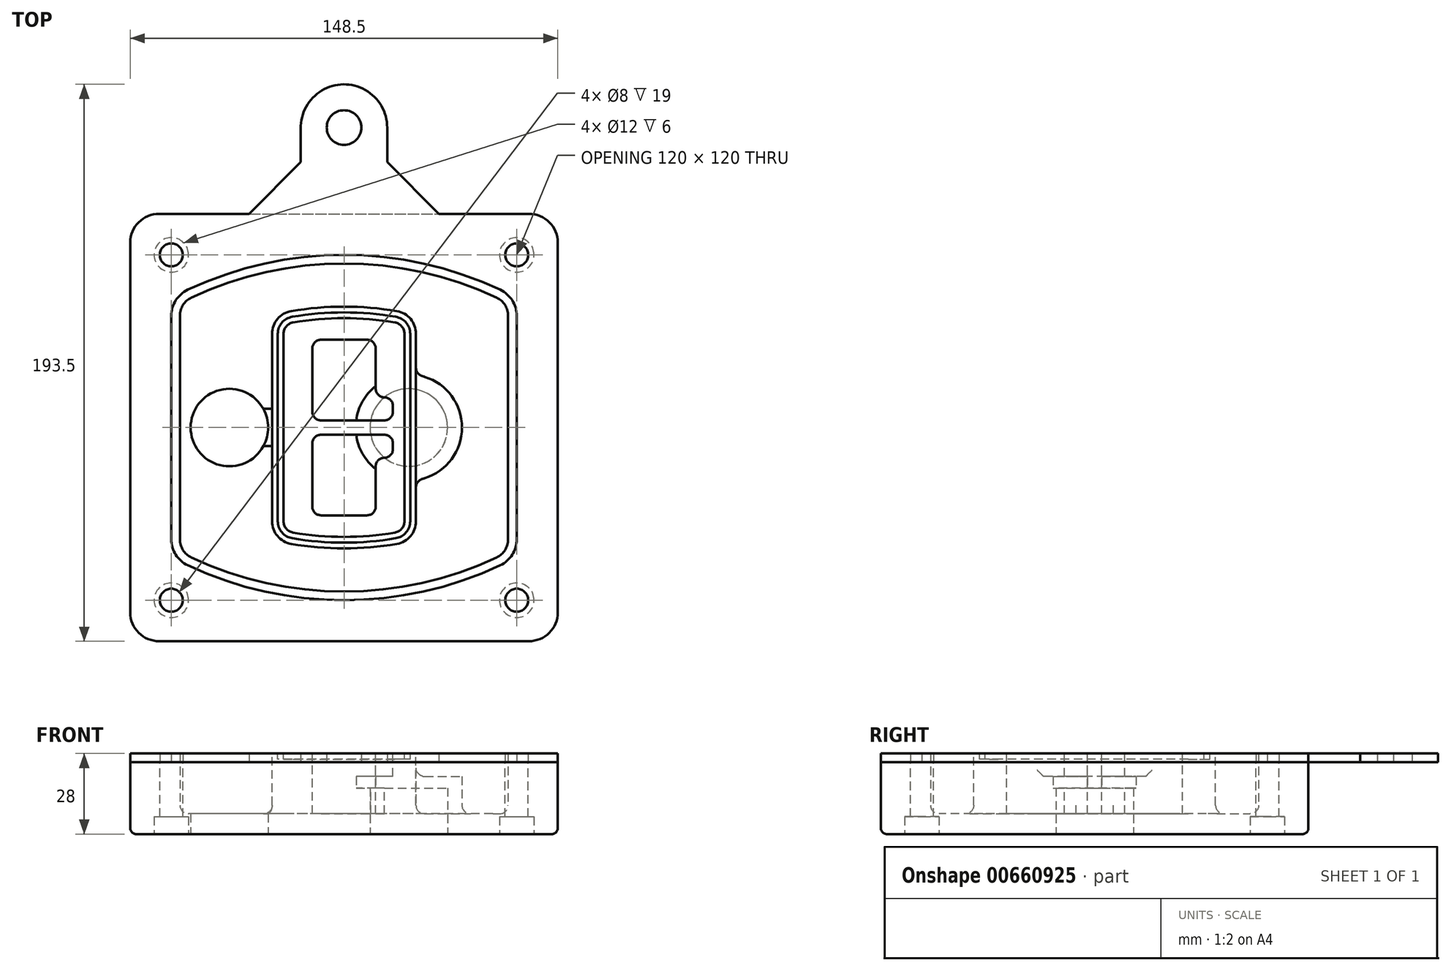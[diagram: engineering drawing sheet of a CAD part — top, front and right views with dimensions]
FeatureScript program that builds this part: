
annotation { "Feature Type Name" : "Feature", "Feature Type Description" : "" }
export const myFeature = defineFeature(function(context is Context, id is Id, definition is map)
    precondition{}
    {
        {
            var Q0;
            Q0=qCreatedBy(makeId("Top.planeOp"),FACE);
            var sketch = newSketch(context, id + "F0", { "sketchPlane" : qUnion([Q0])});
            skPoint(sketch, "E0.rect.middle", {"position": v(0, 0) * mm});
            skLineSegment(sketch, "E1.bottom", {"start": v(-64.25, -74.25) * mm, "end": v(64.25, -74.25) * mm});
            skLineSegment(sketch, "E1.top", {"start": v(-64.25, 74.25) * mm, "end": v(64.25, 74.25) * mm});
            skLineSegment(sketch, "E1.left", {"start": v(-74.25, -64.25) * mm, "end": v(-74.25, 64.25) * mm});
            skLineSegment(sketch, "E1.right", {"start": v(74.25, -64.25) * mm, "end": v(74.25, 64.25) * mm});
            skLineSegment(sketch, "E2", {"start": v(-74.25, 74.25) * mm, "end": v(74.25, -74.25) * mm, "construction": true});
            skLineSegment(sketch, "E3", {"start": v(74.25, 74.25) * mm, "end": v(-74.25, -74.25) * mm, "construction": true});
            skCircle(sketch, "E4", {"center": v(-60, 60) * mm, "radius": 4 * mm});
            skCircle(sketch, "E5", {"center": v(60, 60) * mm, "radius": 4 * mm});
            skCircle(sketch, "E6", {"center": v(60, -60) * mm, "radius": 4 * mm});
            skCircle(sketch, "E7", {"center": v(-60, -60) * mm, "radius": 4 * mm});
            skLineSegment(sketch, "E8", {"start": v(-60, 60) * mm, "end": v(60, 60) * mm, "construction": true});
            skLineSegment(sketch, "E9", {"start": v(60, 60) * mm, "end": v(60, -60) * mm, "construction": true});
            skLineSegment(sketch, "E10", {"start": v(60, -60) * mm, "end": v(-60, -60) * mm, "construction": true});
            skLineSegment(sketch, "E11", {"start": v(-60, -60) * mm, "end": v(-60, 60) * mm, "construction": true});
            skLineSegment(sketch, "E12", {"start": v(-60, 38.83) * mm, "end": v(-60, -38.83) * mm});
            skLineSegment(sketch, "E13", {"start": v(60, 38.83) * mm, "end": v(60, -38.83) * mm});
            skArc(sketch, "E14", {"start": v(54.26, 47.88) * mm, "mid": v(0, 60) * mm, "end": v(-54.26, 47.88) * mm});
            skArc(sketch, "E15", {"start": v(-54.26, -47.88) * mm, "mid": v(0, -60) * mm, "end": v(54.26, -47.88) * mm});
            skLineSegment(sketch, "E16", {"start": v(-60, 0) * mm, "end": v(60, 0) * mm, "construction": true});
            skPoint(sketch, "E17.visualSharp", {"position": v(-60, -45) * mm});
            skArc(sketch, "E17.filletArc", {"start": v(-60, -38.83) * mm, "mid": v(-58.44, -44.2) * mm, "end": v(-54.26, -47.88) * mm});
            skPoint(sketch, "E18.visualSharp", {"position": v(-60, 45) * mm});
            skArc(sketch, "E18.filletArc", {"start": v(-54.26, 47.88) * mm, "mid": v(-58.44, 44.2) * mm, "end": v(-60, 38.83) * mm});
            skPoint(sketch, "E19.visualSharp", {"position": v(60, 45) * mm});
            skArc(sketch, "E19.filletArc", {"start": v(60, 38.83) * mm, "mid": v(58.44, 44.2) * mm, "end": v(54.26, 47.88) * mm});
            skPoint(sketch, "E20.visualSharp", {"position": v(60, -45) * mm});
            skArc(sketch, "E20.filletArc", {"start": v(54.26, -47.88) * mm, "mid": v(58.44, -44.2) * mm, "end": v(60, -38.83) * mm});
            skPoint(sketch, "E21.visualSharp", {"position": v(-74.25, 74.25) * mm});
            skArc(sketch, "E21.filletArc", {"start": v(-64.25, 74.25) * mm, "mid": v(-71.32, 71.32) * mm, "end": v(-74.25, 64.25) * mm});
            skPoint(sketch, "E22.visualSharp", {"position": v(74.25, 74.25) * mm});
            skArc(sketch, "E22.filletArc", {"start": v(74.25, 64.25) * mm, "mid": v(71.32, 71.32) * mm, "end": v(64.25, 74.25) * mm});
            skPoint(sketch, "E23.visualSharp", {"position": v(74.25, -74.25) * mm});
            skArc(sketch, "E23.filletArc", {"start": v(64.25, -74.25) * mm, "mid": v(71.32, -71.32) * mm, "end": v(74.25, -64.25) * mm});
            skPoint(sketch, "E24.visualSharp", {"position": v(-74.25, -74.25) * mm});
            skArc(sketch, "E24.filletArc", {"start": v(-74.25, -64.25) * mm, "mid": v(-71.32, -71.32) * mm, "end": v(-64.25, -74.25) * mm});
            skArc(sketch, "E25.0", {"start": v(57, 38.83) * mm, "mid": v(55.9, 42.58) * mm, "end": v(52.98, 45.17) * mm});
            skLineSegment(sketch, "E25.1", {"start": v(57, 38.83) * mm, "end": v(57, -38.83) * mm});
            skArc(sketch, "E25.2", {"start": v(52.98, -45.17) * mm, "mid": v(55.9, -42.58) * mm, "end": v(57, -38.83) * mm});
            skArc(sketch, "E25.3", {"start": v(-52.98, -45.17) * mm, "mid": v(0, -57) * mm, "end": v(52.98, -45.17) * mm});
            skArc(sketch, "E25.4", {"start": v(-57, -38.83) * mm, "mid": v(-55.9, -42.58) * mm, "end": v(-52.98, -45.17) * mm});
            skArc(sketch, "E25.5", {"start": v(52.98, 45.17) * mm, "mid": v(0, 57) * mm, "end": v(-52.98, 45.17) * mm});
            skLineSegment(sketch, "E25.6", {"start": v(-57, 38.83) * mm, "end": v(-57, -38.83) * mm});
            skArc(sketch, "E25.7", {"start": v(-52.98, 45.17) * mm, "mid": v(-55.9, 42.58) * mm, "end": v(-57, 38.83) * mm});
            skArc(sketch, "E26.0", {"start": v(-55.96, 51.5) * mm, "mid": v(-61.82, 46.33) * mm, "end": v(-64, 38.83) * mm});
            skArc(sketch, "E26.1", {"start": v(55.96, 51.5) * mm, "mid": v(0, 64) * mm, "end": v(-55.96, 51.5) * mm});
            skArc(sketch, "E26.2", {"start": v(64, 38.83) * mm, "mid": v(61.82, 46.33) * mm, "end": v(55.96, 51.5) * mm});
            skLineSegment(sketch, "E26.3", {"start": v(64, 38.83) * mm, "end": v(64, -38.83) * mm});
            skArc(sketch, "E26.4", {"start": v(55.96, -51.5) * mm, "mid": v(61.82, -46.33) * mm, "end": v(64, -38.83) * mm});
            skLineSegment(sketch, "E26.5", {"start": v(-64, 38.83) * mm, "end": v(-64, -38.83) * mm});
            skArc(sketch, "E26.6", {"start": v(-55.96, -51.5) * mm, "mid": v(0, -64) * mm, "end": v(55.96, -51.5) * mm});
            skArc(sketch, "E26.7", {"start": v(-64, -38.83) * mm, "mid": v(-61.82, -46.33) * mm, "end": v(-55.96, -51.5) * mm});
            skSolve(sketch);
        }
        {
            var Q0;
            Q0=makeQuery(id+"F0.imprint","IMPRINT",FACE,{"disambiguationData":[TD([[makeQuery(id+"F0.imprint","IMPRINT",EDGE,{"derivedFrom":sQuery(id+"F0.wireOp",EDGE,"E1.bottom")}),1.0]])]});
            var Q1;
            Q1=makeQuery(id+"F0.imprint","IMPRINT",FACE,{"disambiguationData":[TD([[makeQuery(id+"F0.imprint","IMPRINT",EDGE,{"derivedFrom":sQuery(id+"F0.wireOp",EDGE,"E12")}),1.0]])]});
            var Q2;
            Q2=makeQuery(id+"F0.imprint","IMPRINT",FACE,{"disambiguationData":[TD([[makeQuery(id+"F0.imprint","IMPRINT",EDGE,{"derivedFrom":sQuery(id+"F0.wireOp",EDGE,"E25.0")}),1.0]])]});
            var Q3;
            Q3=makeQuery(id+"F0.imprint","IMPRINT",FACE,{"disambiguationData":[TD([[makeQuery(id+"F0.imprint","IMPRINT",EDGE,{"derivedFrom":sQuery(id+"F0.wireOp",EDGE,"E12")}),-1.0]])]});
            extrude(context, id + "F1", {"entities" : qUnion([Q0, Q1, Q2, Q3]), "oppositeDirection" : true, "depth" : 25 * mm});
        }
        {
            var Q0;
            Q0=makeQuery(id+"F0.imprint","IMPRINT",FACE,{"disambiguationData":[TD([[makeQuery(id+"F0.imprint","IMPRINT",EDGE,{"derivedFrom":sQuery(id+"F0.wireOp",EDGE,"E12")}),1.0]])]});
            extrude(context, id + "F2", {"entities" : qUnion([Q0]), "operationType" : NewBodyOperationType.ADD, "depth" : 3 * mm});
        }
        {
            var Q0;
            Q0=makeQuery(id+"F0.imprint","IMPRINT",FACE,{"disambiguationData":[TD([[makeQuery(id+"F0.imprint","IMPRINT",EDGE,{"derivedFrom":sQuery(id+"F0.wireOp",EDGE,"E25.0")}),1.0]])]});
            extrude(context, id + "F3", {"entities" : qUnion([Q0]), "operationType" : NewBodyOperationType.REMOVE, "oppositeDirection" : true, "depth" : 18 * mm});
        }
        {
            var Q0;
            Q0=makeQuery(id+"F2.opExtrude","CAP_FACE",FACE,{"disambiguationData":[OSD([sQuery(id+"F0.wireOp",EDGE,"E12"),sQuery(id+"F0.wireOp",EDGE,"E13"),sQuery(id+"F0.wireOp",EDGE,"E14"),sQuery(id+"F0.wireOp",EDGE,"E15"),sQuery(id+"F0.wireOp",EDGE,"E17.filletArc"),sQuery(id+"F0.wireOp",EDGE,"E18.filletArc"),sQuery(id+"F0.wireOp",EDGE,"E19.filletArc"),sQuery(id+"F0.wireOp",EDGE,"E20.filletArc"),sQuery(id+"F0.wireOp",EDGE,"E25.0"),sQuery(id+"F0.wireOp",EDGE,"E25.1"),sQuery(id+"F0.wireOp",EDGE,"E25.2"),sQuery(id+"F0.wireOp",EDGE,"E25.3"),sQuery(id+"F0.wireOp",EDGE,"E25.4"),sQuery(id+"F0.wireOp",EDGE,"E25.5"),sQuery(id+"F0.wireOp",EDGE,"E25.6"),sQuery(id+"F0.wireOp",EDGE,"E25.7")])],"isStart":false});
            var sketch = newSketch(context, id + "F4", { "sketchPlane" : qUnion([Q0])});
            skArc(sketch, "E27.0", {"start": v(-18.34, -40.45) * mm, "mid": v(0, -42) * mm, "end": v(18.34, -40.45) * mm});
            skArc(sketch, "E28.0", {"start": v(18.34, 40.45) * mm, "mid": v(0, 42) * mm, "end": v(-18.34, 40.45) * mm});
            skLineSegment(sketch, "E29", {"start": v(-25, 32.57) * mm, "end": v(-25, -32.57) * mm});
            skLineSegment(sketch, "E30", {"start": v(25, 32.57) * mm, "end": v(25, -32.57) * mm});
            skLineSegment(sketch, "E31", {"start": v(-25, 39.1) * mm, "end": v(25, 39.1) * mm, "construction": true});
            skLineSegment(sketch, "E32", {"start": v(-25, -39.1) * mm, "end": v(25, -39.1) * mm, "construction": true});
            skPoint(sketch, "E33.visualSharp", {"position": v(-25, 39.1) * mm});
            skArc(sketch, "E33.filletArc", {"start": v(-18.34, 40.45) * mm, "mid": v(-23.11, 37.73) * mm, "end": v(-25, 32.57) * mm});
            skPoint(sketch, "E34.visualSharp", {"position": v(25, 39.1) * mm});
            skArc(sketch, "E34.filletArc", {"start": v(25, 32.57) * mm, "mid": v(23.11, 37.73) * mm, "end": v(18.34, 40.45) * mm});
            skPoint(sketch, "E35.visualSharp", {"position": v(25, -39.1) * mm});
            skArc(sketch, "E35.filletArc", {"start": v(18.34, -40.45) * mm, "mid": v(23.11, -37.73) * mm, "end": v(25, -32.57) * mm});
            skPoint(sketch, "E36.visualSharp", {"position": v(-25, -39.1) * mm});
            skArc(sketch, "E36.filletArc", {"start": v(-25, -32.57) * mm, "mid": v(-23.11, -37.73) * mm, "end": v(-18.34, -40.45) * mm});
            skArc(sketch, "E37.0", {"start": v(52.98, 45.17) * mm, "mid": v(0, 57) * mm, "end": v(-52.98, 45.17) * mm});
            skArc(sketch, "E37.1", {"start": v(-52.98, 45.17) * mm, "mid": v(-55.9, 42.58) * mm, "end": v(-57, 38.83) * mm});
            skLineSegment(sketch, "E37.2", {"start": v(-57, 38.83) * mm, "end": v(-57, -38.83) * mm});
            skArc(sketch, "E37.3", {"start": v(-57, -38.83) * mm, "mid": v(-55.9, -42.58) * mm, "end": v(-52.98, -45.17) * mm});
            skArc(sketch, "E37.4", {"start": v(-52.98, -45.17) * mm, "mid": v(0, -57) * mm, "end": v(52.98, -45.17) * mm});
            skArc(sketch, "E37.5", {"start": v(52.98, -45.17) * mm, "mid": v(55.9, -42.58) * mm, "end": v(57, -38.83) * mm});
            skLineSegment(sketch, "E37.6", {"start": v(57, 38.83) * mm, "end": v(57, -38.83) * mm});
            skArc(sketch, "E37.7", {"start": v(57, 38.83) * mm, "mid": v(55.9, 42.58) * mm, "end": v(52.98, 45.17) * mm});
            skLineSegment(sketch, "E38.0", {"start": v(23, 32.57) * mm, "end": v(23, -32.57) * mm});
            skArc(sketch, "E38.1", {"start": v(18, -38.48) * mm, "mid": v(21.58, -36.44) * mm, "end": v(23, -32.57) * mm});
            skArc(sketch, "E38.2", {"start": v(-18, -38.48) * mm, "mid": v(0, -40) * mm, "end": v(18, -38.48) * mm});
            skArc(sketch, "E38.3", {"start": v(-23, -32.57) * mm, "mid": v(-21.58, -36.44) * mm, "end": v(-18, -38.48) * mm});
            skLineSegment(sketch, "E38.4", {"start": v(-23, 32.57) * mm, "end": v(-23, -32.57) * mm});
            skArc(sketch, "E38.5", {"start": v(23, 32.57) * mm, "mid": v(21.58, 36.44) * mm, "end": v(18, 38.48) * mm});
            skArc(sketch, "E38.6", {"start": v(-18, 38.48) * mm, "mid": v(-21.58, 36.44) * mm, "end": v(-23, 32.57) * mm});
            skArc(sketch, "E38.7", {"start": v(18, 38.48) * mm, "mid": v(0, 40) * mm, "end": v(-18, 38.48) * mm});
            skArc(sketch, "E39.0", {"start": v(21, 32.57) * mm, "mid": v(20.06, 35.15) * mm, "end": v(17.67, 36.5) * mm});
            skLineSegment(sketch, "E39.1", {"start": v(21, 32.57) * mm, "end": v(21, -32.57) * mm});
            skArc(sketch, "E39.2", {"start": v(17.67, -36.5) * mm, "mid": v(20.06, -35.15) * mm, "end": v(21, -32.57) * mm});
            skArc(sketch, "E39.3", {"start": v(-17.67, -36.5) * mm, "mid": v(0, -38) * mm, "end": v(17.67, -36.5) * mm});
            skArc(sketch, "E39.4", {"start": v(-21, -32.57) * mm, "mid": v(-20.06, -35.15) * mm, "end": v(-17.67, -36.5) * mm});
            skArc(sketch, "E39.5", {"start": v(17.67, 36.5) * mm, "mid": v(0, 38) * mm, "end": v(-17.67, 36.5) * mm});
            skLineSegment(sketch, "E39.6", {"start": v(-21, 32.57) * mm, "end": v(-21, -32.57) * mm});
            skArc(sketch, "E39.7", {"start": v(-17.67, 36.5) * mm, "mid": v(-20.06, 35.15) * mm, "end": v(-21, 32.57) * mm});
            skLineSegment(sketch, "E40", {"start": v(-25, 0) * mm, "end": v(25, 0) * mm, "construction": true});
            skLineSegment(sketch, "E41", {"start": v(-11, 5.5) * mm, "end": v(-11, 27.5) * mm});
            skLineSegment(sketch, "E42", {"start": v(-8, 30.5) * mm, "end": v(8, 30.5) * mm});
            skLineSegment(sketch, "E43", {"start": v(11, 27.5) * mm, "end": v(11, 13.5) * mm});
            skLineSegment(sketch, "E44", {"start": v(14, 10.5) * mm, "end": v(14, 10.5) * mm});
            skLineSegment(sketch, "E45", {"start": v(17, 7.5) * mm, "end": v(17, 5.5) * mm});
            skLineSegment(sketch, "E46", {"start": v(14, 2.5) * mm, "end": v(-8, 2.5) * mm});
            skPoint(sketch, "E47.visualSharp", {"position": v(-11, 30.5) * mm});
            skArc(sketch, "E47.filletArc", {"start": v(-8, 30.5) * mm, "mid": v(-10.12, 29.62) * mm, "end": v(-11, 27.5) * mm});
            skPoint(sketch, "E48.visualSharp", {"position": v(11, 30.5) * mm});
            skArc(sketch, "E48.filletArc", {"start": v(11, 27.5) * mm, "mid": v(10.12, 29.62) * mm, "end": v(8, 30.5) * mm});
            skPoint(sketch, "E49.visualSharp", {"position": v(11, 10.5) * mm});
            skArc(sketch, "E49.filletArc", {"start": v(11, 13.5) * mm, "mid": v(11.88, 11.38) * mm, "end": v(14, 10.5) * mm});
            skPoint(sketch, "E50.visualSharp", {"position": v(17, 10.5) * mm});
            skArc(sketch, "E50.filletArc", {"start": v(17, 7.5) * mm, "mid": v(16.12, 9.62) * mm, "end": v(14, 10.5) * mm});
            skPoint(sketch, "E51.visualSharp", {"position": v(17, 2.5) * mm});
            skArc(sketch, "E51.filletArc", {"start": v(14, 2.5) * mm, "mid": v(16.12, 3.38) * mm, "end": v(17, 5.5) * mm});
            skPoint(sketch, "E52.visualSharp", {"position": v(-11, 2.5) * mm});
            skArc(sketch, "E52.filletArc", {"start": v(-11, 5.5) * mm, "mid": v(-10.12, 3.38) * mm, "end": v(-8, 2.5) * mm});
            skLineSegment(sketch, "E53.0.MirrorCS", {"start": v(14, -2.5) * mm, "end": v(-8, -2.5) * mm});
            skArc(sketch, "E54.0.MirrorCS", {"start": v(-11, -5.5) * mm, "mid": v(-10.12, -3.38) * mm, "end": v(-8, -2.5) * mm});
            skLineSegment(sketch, "E55.0.MirrorCS", {"start": v(-11, -5.5) * mm, "end": v(-11, -27.5) * mm});
            skArc(sketch, "E56.0.MirrorCS", {"start": v(-8, -30.5) * mm, "mid": v(-10.12, -29.62) * mm, "end": v(-11, -27.5) * mm});
            skLineSegment(sketch, "E57.0.MirrorCS", {"start": v(-8, -30.5) * mm, "end": v(8, -30.5) * mm});
            skArc(sketch, "E58.0.MirrorCS", {"start": v(11, -27.5) * mm, "mid": v(10.12, -29.62) * mm, "end": v(8, -30.5) * mm});
            skLineSegment(sketch, "E59.0.MirrorCS", {"start": v(11, -27.5) * mm, "end": v(11, -13.5) * mm});
            skArc(sketch, "E60.0.MirrorCS", {"start": v(11, -13.5) * mm, "mid": v(11.88, -11.38) * mm, "end": v(14, -10.5) * mm});
            skArc(sketch, "E61.0.MirrorCS", {"start": v(17, -7.5) * mm, "mid": v(16.12, -9.62) * mm, "end": v(14, -10.5) * mm});
            skLineSegment(sketch, "E62.0.MirrorCS", {"start": v(17, -7.5) * mm, "end": v(17, -5.5) * mm});
            skArc(sketch, "E63.0.MirrorCS", {"start": v(14, -2.5) * mm, "mid": v(16.12, -3.38) * mm, "end": v(17, -5.5) * mm});
            skSolve(sketch);
        }
        {
            var Q0;
            Q0=makeQuery(id+"F4.imprint","IMPRINT",FACE,{"disambiguationData":[TD([[makeQuery(id+"F4.imprint","IMPRINT",EDGE,{"derivedFrom":sQuery(id+"F4.wireOp",EDGE,"E27.0")}),1.0]])]});
            var Q1;
            Q1=makeQuery(id+"F4.imprint","IMPRINT",FACE,{"disambiguationData":[TD([[makeQuery(id+"F4.imprint","IMPRINT",EDGE,{"derivedFrom":sQuery(id+"F4.wireOp",EDGE,"E38.0")}),-1.0]])]});
            var Q2;
            Q2=makeQuery(id+"F4.imprint","IMPRINT",FACE,{"disambiguationData":[TD([[makeQuery(id+"F4.imprint","IMPRINT",EDGE,{"derivedFrom":sQuery(id+"F4.wireOp",EDGE,"E39.0")}),1.0]])]});
            extrude(context, id + "F5", {"entities" : qUnion([Q0, Q1, Q2]), "operationType" : NewBodyOperationType.ADD, "endBound" : BoundingType.UP_TO_NEXT, "oppositeDirection" : true, "depth" : 25 * mm});
        }
        {
            var Q0;
            Q0=makeQuery(id+"F4.imprint","IMPRINT",FACE,{"disambiguationData":[TD([[makeQuery(id+"F4.imprint","IMPRINT",EDGE,{"derivedFrom":sQuery(id+"F4.wireOp",EDGE,"E38.0")}),-1.0]])]});
            extrude(context, id + "F6", {"entities" : qUnion([Q0]), "operationType" : NewBodyOperationType.REMOVE, "oppositeDirection" : true, "depth" : 2 * mm});
        }
        {
            var Q0;
            Q0=makeQuery(id+"F1.opExtrude","CAP_FACE",FACE,{"disambiguationData":[OSD([sQuery(id+"F0.wireOp",EDGE,"E1.bottom"),sQuery(id+"F0.wireOp",EDGE,"E1.top"),sQuery(id+"F0.wireOp",EDGE,"E1.left"),sQuery(id+"F0.wireOp",EDGE,"E1.right"),sQuery(id+"F0.wireOp",EDGE,"E4"),sQuery(id+"F0.wireOp",EDGE,"E5"),sQuery(id+"F0.wireOp",EDGE,"E6"),sQuery(id+"F0.wireOp",EDGE,"E7"),sQuery(id+"F0.wireOp",EDGE,"E21.filletArc"),sQuery(id+"F0.wireOp",EDGE,"E22.filletArc"),sQuery(id+"F0.wireOp",EDGE,"E23.filletArc"),sQuery(id+"F0.wireOp",EDGE,"E24.filletArc")])],"isStart":false});
            var sketch = newSketch(context, id + "F7", { "sketchPlane" : qUnion([Q0])});
            skCircle(sketch, "E64", {"center": v(22.5, 0) * mm, "radius": 13.47 * mm});
            skCircle(sketch, "E65", {"center": v(-39.81, 0) * mm, "radius": 13.47 * mm});
            skLineSegment(sketch, "E66", {"start": v(74.25, 0) * mm, "end": v(-74.25, 0) * mm});
            skCircle(sketch, "E67", {"center": v(22.5, 0) * mm, "radius": 18.47 * mm});
            skCircle(sketch, "E68", {"center": v(60, -60) * mm, "radius": 6 * mm});
            skCircle(sketch, "E69", {"center": v(-60, -60) * mm, "radius": 6 * mm});
            skCircle(sketch, "E70", {"center": v(-60, 60) * mm, "radius": 6 * mm});
            skCircle(sketch, "E71", {"center": v(60, 60) * mm, "radius": 6 * mm});
            skSolve(sketch);
        }
        {
            var Q0;
            {var subQ1=sQuery(id+"F7.wireOp",EDGE,"E66");var subQ4=sQuery(id+"F7.wireOp",EDGE,"E64");var subQ6=makeQuery(id+"F7.imprint","INTERSECT",VERTEX,{"disambiguationData":[OD(0.0)],"derivedFrom":[subQ4,subQ1]});Q0=makeQuery(id+"F7.imprint","IMPRINT",FACE,{"disambiguationData":[TD([[makeQuery(id+"F7.imprint","IMPRINT",EDGE,{"disambiguationData":[TD([[subQ6,-1.0]])],"derivedFrom":subQ4}),-1.0]])]});}
            var Q1;
            {var subQ0=sQuery(id+"F7.wireOp",EDGE,"E66");var subQ1=sQuery(id+"F7.wireOp",EDGE,"E64");var subQ3=makeQuery(id+"F7.imprint","INTERSECT",VERTEX,{"disambiguationData":[OD(0.0)],"derivedFrom":[subQ1,subQ0]});Q1=makeQuery(id+"F7.imprint","IMPRINT",FACE,{"disambiguationData":[TD([[makeQuery(id+"F7.imprint","IMPRINT",EDGE,{"disambiguationData":[TD([[subQ3,-1.0]])],"derivedFrom":subQ1}),1.0]])]});}
            var Q2;
            {var subQ0=sQuery(id+"F7.wireOp",EDGE,"E66");var subQ1=sQuery(id+"F7.wireOp",EDGE,"E64");var subQ3=makeQuery(id+"F7.imprint","INTERSECT",VERTEX,{"disambiguationData":[OD(0.0)],"derivedFrom":[subQ1,subQ0]});Q2=makeQuery(id+"F7.imprint","IMPRINT",FACE,{"disambiguationData":[TD([[makeQuery(id+"F7.imprint","IMPRINT",EDGE,{"disambiguationData":[TD([[subQ3,1.0]])],"derivedFrom":subQ1}),1.0]])]});}
            var Q3;
            {var subQ1=sQuery(id+"F7.wireOp",EDGE,"E66");var subQ4=sQuery(id+"F7.wireOp",EDGE,"E64");var subQ6=makeQuery(id+"F7.imprint","INTERSECT",VERTEX,{"disambiguationData":[OD(0.0)],"derivedFrom":[subQ4,subQ1]});Q3=makeQuery(id+"F7.imprint","IMPRINT",FACE,{"disambiguationData":[TD([[makeQuery(id+"F7.imprint","IMPRINT",EDGE,{"disambiguationData":[TD([[subQ6,1.0]])],"derivedFrom":subQ4}),-1.0]])]});}
            extrude(context, id + "F8", {"entities" : qUnion([Q0, Q1, Q2, Q3]), "operationType" : NewBodyOperationType.ADD, "oppositeDirection" : true, "depth" : 20 * mm});
        }
        {
            var Q0;
            {var subQ0=sQuery(id+"F7.wireOp",EDGE,"E66");var subQ1=sQuery(id+"F7.wireOp",EDGE,"E64");var subQ3=makeQuery(id+"F7.imprint","INTERSECT",VERTEX,{"disambiguationData":[OD(0.0)],"derivedFrom":[subQ1,subQ0]});Q0=makeQuery(id+"F7.imprint","IMPRINT",FACE,{"disambiguationData":[TD([[makeQuery(id+"F7.imprint","IMPRINT",EDGE,{"disambiguationData":[TD([[subQ3,-1.0]])],"derivedFrom":subQ1}),1.0]])]});}
            var Q1;
            {var subQ0=sQuery(id+"F7.wireOp",EDGE,"E66");var subQ1=sQuery(id+"F7.wireOp",EDGE,"E64");var subQ3=makeQuery(id+"F7.imprint","INTERSECT",VERTEX,{"disambiguationData":[OD(0.0)],"derivedFrom":[subQ1,subQ0]});Q1=makeQuery(id+"F7.imprint","IMPRINT",FACE,{"disambiguationData":[TD([[makeQuery(id+"F7.imprint","IMPRINT",EDGE,{"disambiguationData":[TD([[subQ3,1.0]])],"derivedFrom":subQ1}),1.0]])]});}
            extrude(context, id + "F9", {"entities" : qUnion([Q0, Q1]), "operationType" : NewBodyOperationType.REMOVE, "oppositeDirection" : true, "depth" : 16 * mm});
        }
        {
            var Q0;
            {var subQ0=sQuery(id+"F7.wireOp",EDGE,"E66");var subQ1=sQuery(id+"F7.wireOp",EDGE,"E65");var subQ3=makeQuery(id+"F7.imprint","INTERSECT",VERTEX,{"disambiguationData":[OD(0.0)],"derivedFrom":[subQ1,subQ0]});Q0=makeQuery(id+"F7.imprint","IMPRINT",FACE,{"disambiguationData":[TD([[makeQuery(id+"F7.imprint","IMPRINT",EDGE,{"disambiguationData":[TD([[subQ3,-1.0]])],"derivedFrom":subQ1}),1.0]])]});}
            var Q1;
            {var subQ0=sQuery(id+"F7.wireOp",EDGE,"E66");var subQ1=sQuery(id+"F7.wireOp",EDGE,"E65");var subQ3=makeQuery(id+"F7.imprint","INTERSECT",VERTEX,{"disambiguationData":[OD(0.0)],"derivedFrom":[subQ1,subQ0]});Q1=makeQuery(id+"F7.imprint","IMPRINT",FACE,{"disambiguationData":[TD([[makeQuery(id+"F7.imprint","IMPRINT",EDGE,{"disambiguationData":[TD([[subQ3,1.0]])],"derivedFrom":subQ1}),1.0]])]});}
            extrude(context, id + "F10", {"entities" : qUnion([Q0, Q1]), "operationType" : NewBodyOperationType.REMOVE, "oppositeDirection" : true, "depth" : 25 * mm});
        }
        {
            var Q0;
            Q0=makeQuery(id+"F7.imprint","IMPRINT",FACE,{"disambiguationData":[TD([[makeQuery(id+"F7.imprint","IMPRINT",EDGE,{"derivedFrom":sQuery(id+"F7.wireOp",EDGE,"E68")}),1.0]])]});
            var Q1;
            Q1=makeQuery(id+"F7.imprint","IMPRINT",FACE,{"disambiguationData":[TD([[makeQuery(id+"F7.imprint","IMPRINT",EDGE,{"derivedFrom":makeQuery(id+"F1.opExtrude","CAP_EDGE",EDGE,{"disambiguationData":[OSD([sQuery(id+"F0.wireOp",EDGE,"E5")])],"isStart":false})}),-1.0]])]});
            var Q2;
            Q2=makeQuery(id+"F7.imprint","IMPRINT",FACE,{"disambiguationData":[TD([[makeQuery(id+"F7.imprint","IMPRINT",EDGE,{"derivedFrom":sQuery(id+"F7.wireOp",EDGE,"E69")}),1.0]])]});
            var Q3;
            Q3=makeQuery(id+"F7.imprint","IMPRINT",FACE,{"disambiguationData":[TD([[makeQuery(id+"F7.imprint","IMPRINT",EDGE,{"derivedFrom":makeQuery(id+"F1.opExtrude","CAP_EDGE",EDGE,{"disambiguationData":[OSD([sQuery(id+"F0.wireOp",EDGE,"E4")])],"isStart":false})}),-1.0]])]});
            var Q4;
            Q4=makeQuery(id+"F7.imprint","IMPRINT",FACE,{"disambiguationData":[TD([[makeQuery(id+"F7.imprint","IMPRINT",EDGE,{"derivedFrom":sQuery(id+"F7.wireOp",EDGE,"E70")}),1.0]])]});
            var Q5;
            Q5=makeQuery(id+"F7.imprint","IMPRINT",FACE,{"disambiguationData":[TD([[makeQuery(id+"F7.imprint","IMPRINT",EDGE,{"derivedFrom":makeQuery(id+"F1.opExtrude","CAP_EDGE",EDGE,{"disambiguationData":[OSD([sQuery(id+"F0.wireOp",EDGE,"E7")])],"isStart":false})}),-1.0]])]});
            var Q6;
            Q6=makeQuery(id+"F7.imprint","IMPRINT",FACE,{"disambiguationData":[TD([[makeQuery(id+"F7.imprint","IMPRINT",EDGE,{"derivedFrom":sQuery(id+"F7.wireOp",EDGE,"E71")}),1.0]])]});
            var Q7;
            Q7=makeQuery(id+"F7.imprint","IMPRINT",FACE,{"disambiguationData":[TD([[makeQuery(id+"F7.imprint","IMPRINT",EDGE,{"derivedFrom":makeQuery(id+"F1.opExtrude","CAP_EDGE",EDGE,{"disambiguationData":[OSD([sQuery(id+"F0.wireOp",EDGE,"E6")])],"isStart":false})}),-1.0]])]});
            extrude(context, id + "F11", {"entities" : qUnion([Q0, Q1, Q2, Q3, Q4, Q5, Q6, Q7]), "operationType" : NewBodyOperationType.REMOVE, "oppositeDirection" : true, "depth" : 6 * mm});
        }
        {
            var Q0;
            Q0=makeQuery(id+"F9.boolean.opBoolean","COPY",FACE,{"derivedFrom":makeQuery(id+"F9.opExtrude","CAP_FACE",FACE,{"disambiguationData":[OSD([sQuery(id+"F7.wireOp",EDGE,"E64")])],"isStart":false})});
            var sketch = newSketch(context, id + "F12", { "sketchPlane" : qUnion([Q0])});
            skArc(sketch, "E72.0", {"start": v(11, 14.45) * mm, "mid": v(6.45, 9.13) * mm, "end": v(4.2, 2.5) * mm});
            skArc(sketch, "E72.1", {"start": v(4.2, -2.5) * mm, "mid": v(6.45, -9.13) * mm, "end": v(11, -14.45) * mm});
            skLineSegment(sketch, "E73", {"start": v(4.2, -2.5) * mm, "end": v(14, -2.5) * mm});
            skLineSegment(sketch, "E74.0", {"start": v(14, 2.5) * mm, "end": v(4.2, 2.5) * mm});
            skArc(sketch, "E74.1", {"start": v(14, 2.5) * mm, "mid": v(16.12, 3.38) * mm, "end": v(17, 5.5) * mm});
            skLineSegment(sketch, "E74.2", {"start": v(17, 7.5) * mm, "end": v(17, 5.5) * mm});
            skArc(sketch, "E74.3", {"start": v(17, 7.5) * mm, "mid": v(16.12, 9.62) * mm, "end": v(14, 10.5) * mm});
            skArc(sketch, "E74.4", {"start": v(11, 13.5) * mm, "mid": v(11.88, 11.38) * mm, "end": v(14, 10.5) * mm});
            skLineSegment(sketch, "E74.5", {"start": v(11, 14.45) * mm, "end": v(11, 13.5) * mm});
            skLineSegment(sketch, "E74.7", {"start": v(14, -2.5) * mm, "end": v(4.2, -2.5) * mm});
            skArc(sketch, "E74.8", {"start": v(14, -2.5) * mm, "mid": v(16.12, -3.38) * mm, "end": v(17, -5.5) * mm});
            skLineSegment(sketch, "E74.9", {"start": v(17, -7.5) * mm, "end": v(17, -5.5) * mm});
            skArc(sketch, "E74.10", {"start": v(17, -7.5) * mm, "mid": v(16.12, -9.62) * mm, "end": v(14, -10.5) * mm});
            skArc(sketch, "E74.11", {"start": v(11, -13.5) * mm, "mid": v(11.88, -11.38) * mm, "end": v(14, -10.5) * mm});
            skLineSegment(sketch, "E74.12", {"start": v(11, -14.45) * mm, "end": v(11, -13.5) * mm});
            skPoint(sketch, "E75.orphan", {"position": v(11, -27.5) * mm});
            skPoint(sketch, "E76.orphan", {"position": v(-8, -2.5) * mm});
            skPoint(sketch, "E77.orphan", {"position": v(-8, 2.5) * mm});
            skPoint(sketch, "E78.orphan", {"position": v(11, 27.5) * mm});
            skSolve(sketch);
        }
        {
            var Q0;
            {var subQ7=sQuery(id+"F12.wireOp",EDGE,"E72.0");var subQ14=sQuery(id+"F12.wireOp",EDGE,"E72.1");var subQ16=sQuery(id+"F12.wireOp",EDGE,"E74.1");var subQ18=sQuery(id+"F12.wireOp",EDGE,"E74.8");Q0=qUnion([makeQuery(id+"F12.imprint","IMPRINT",FACE,{"disambiguationData":[TD([[makeQuery(id+"F12.imprint","IMPRINT",EDGE,{"derivedFrom":subQ7}),1.0]])]}),makeQuery(id+"F12.imprint","IMPRINT",FACE,{"disambiguationData":[TD([[makeQuery(id+"F12.imprint","IMPRINT",EDGE,{"derivedFrom":subQ14}),1.0]])]}),makeQuery(id+"F12.imprint","IMPRINT",FACE,{"disambiguationData":[TD([[makeQuery(id+"F12.imprint","IMPRINT",EDGE,{"derivedFrom":subQ16}),1.0]])]}),makeQuery(id+"F12.imprint","IMPRINT",FACE,{"disambiguationData":[TD([[makeQuery(id+"F12.imprint","IMPRINT",EDGE,{"derivedFrom":subQ18}),-1.0]])]})]);}
            var Q1;
            Q1=makeQuery(id+"F5.boolean.opBoolean","SPLIT",FACE,{"disambiguationData":[TD([makeQuery(id+"F5.opExtrude","SWEPT_FACE",FACE,{"disambiguationData":[OSD([sQuery(id+"F4.wireOp",EDGE,"E41")])]})])],"derivedFrom":makeQuery(id+"F3.boolean.opBoolean","COPY",FACE,{"derivedFrom":makeQuery(id+"F3.opExtrude","CAP_FACE",FACE,{"disambiguationData":[OSD([sQuery(id+"F0.wireOp",EDGE,"E25.0"),sQuery(id+"F0.wireOp",EDGE,"E25.1"),sQuery(id+"F0.wireOp",EDGE,"E25.2"),sQuery(id+"F0.wireOp",EDGE,"E25.3"),sQuery(id+"F0.wireOp",EDGE,"E25.4"),sQuery(id+"F0.wireOp",EDGE,"E25.5"),sQuery(id+"F0.wireOp",EDGE,"E25.6"),sQuery(id+"F0.wireOp",EDGE,"E25.7")])],"isStart":false})})});
            extrude(context, id + "F13", {"entities" : qUnion([Q0]), "operationType" : NewBodyOperationType.REMOVE, "endBound" : BoundingType.UP_TO_SURFACE, "endBoundEntityFace" : qUnion([Q1]), "depth" : 25 * mm});
        }
        {
            var Q0;
            Q0=makeQuery(id+"F3.boolean.opBoolean","COPY",EDGE,{"derivedFrom":makeQuery(id+"F3.opExtrude","CAP_EDGE",EDGE,{"disambiguationData":[OSD([sQuery(id+"F0.wireOp",EDGE,"E25.6")])],"isStart":false})});
            var Q1;
            Q1=makeQuery(id+"F8.boolean.opBoolean","INTERSECT",EDGE,{"derivedFrom":[makeQuery(id+"F5.opExtrude","SWEPT_FACE",FACE,{"disambiguationData":[OSD([sQuery(id+"F4.wireOp",EDGE,"E30")])]}),makeQuery(id+"F8.opExtrude","CAP_FACE",FACE,{"disambiguationData":[OSD([sQuery(id+"F7.wireOp",EDGE,"E67")])],"isStart":false})]});
            var Q2;
            Q2=makeQuery(id+"F8.boolean.opBoolean","INTERSECT",EDGE,{"disambiguationData":[OD(1.0)],"derivedFrom":[makeQuery(id+"F5.opExtrude","SWEPT_FACE",FACE,{"disambiguationData":[OSD([sQuery(id+"F4.wireOp",EDGE,"E30")])]}),makeQuery(id+"F8.opExtrude","SWEPT_FACE",FACE,{"disambiguationData":[OSD([sQuery(id+"F7.wireOp",EDGE,"E67")])]})]});
            var Q3;
            {var subQ0=sQuery(id+"F4.wireOp",EDGE,"E30");Q3=makeQuery(id+"F8.boolean.opBoolean","SPLIT",EDGE,{"disambiguationData":[TD([makeQuery(id+"F5.opExtrude","SWEPT_FACE",FACE,{"disambiguationData":[OSD([sQuery(id+"F4.wireOp",EDGE,"E35.filletArc")])]})])],"derivedFrom":makeQuery(id+"F5.opExtrude","CAP_EDGE",EDGE,{"disambiguationData":[OSD([subQ0])],"isStart":false})});}
            var Q4;
            {var subQ0=sQuery(id+"F0.wireOp",EDGE,"E25.7");var subQ1=sQuery(id+"F0.wireOp",EDGE,"E25.1");var subQ2=sQuery(id+"F0.wireOp",EDGE,"E25.6");var subQ3=sQuery(id+"F0.wireOp",EDGE,"E25.5");var subQ4=sQuery(id+"F0.wireOp",EDGE,"E25.4");var subQ5=sQuery(id+"F0.wireOp",EDGE,"E25.0");var subQ6=sQuery(id+"F0.wireOp",EDGE,"E25.2");var subQ7=sQuery(id+"F0.wireOp",EDGE,"E25.3");Q4=makeQuery(id+"F8.boolean.opBoolean","INTERSECT",EDGE,{"derivedFrom":[makeQuery(id+"F5.boolean.opBoolean","SPLIT",FACE,{"disambiguationData":[TD([makeQuery(id+"F2.opExtrude","SWEPT_FACE",FACE,{"disambiguationData":[OSD([subQ5])]})])],"derivedFrom":makeQuery(id+"F3.boolean.opBoolean","COPY",FACE,{"derivedFrom":makeQuery(id+"F3.opExtrude","CAP_FACE",FACE,{"disambiguationData":[OSD([subQ5,subQ1,subQ6,subQ7,subQ4,subQ3,subQ2,subQ0])],"isStart":false})})}),makeQuery(id+"F8.opExtrude","SWEPT_FACE",FACE,{"disambiguationData":[OSD([sQuery(id+"F7.wireOp",EDGE,"E67")])]})]});}
            var Q5;
            Q5=makeQuery(id+"F8.boolean.opBoolean","INTERSECT",EDGE,{"disambiguationData":[OD(0.0)],"derivedFrom":[makeQuery(id+"F5.opExtrude","SWEPT_FACE",FACE,{"disambiguationData":[OSD([sQuery(id+"F4.wireOp",EDGE,"E30")])]}),makeQuery(id+"F8.opExtrude","SWEPT_FACE",FACE,{"disambiguationData":[OSD([sQuery(id+"F7.wireOp",EDGE,"E67")])]})]});
            fillet(context, id + "F14", {"entities" : qUnion([Q0, Q1, Q2, Q3, Q4, Q5]), "radius" : 3 * mm, "tangentPropagation" : true, "allowEdgeOverflow" : false});
        }
        {
            var Q0;
            Q0=makeQuery(id+"F1.opExtrude","CAP_EDGE",EDGE,{"disambiguationData":[OSD([sQuery(id+"F0.wireOp",EDGE,"E1.bottom")])],"isStart":false});
            fillet(context, id + "F15", {"entities" : qUnion([Q0]), "radius" : 2 * mm, "tangentPropagation" : true, "allowEdgeOverflow" : false});
        }
        {
            var Q0;
            {var subQ0=sQuery(id+"F0.wireOp",EDGE,"E21.filletArc");var subQ1=sQuery(id+"F0.wireOp",EDGE,"E7");var subQ2=sQuery(id+"F0.wireOp",EDGE,"E6");var subQ3=sQuery(id+"F0.wireOp",EDGE,"E5");var subQ4=sQuery(id+"F0.wireOp",EDGE,"E4");var subQ5=sQuery(id+"F0.wireOp",EDGE,"E22.filletArc");var subQ6=sQuery(id+"F0.wireOp",EDGE,"E1.bottom");var subQ7=sQuery(id+"F0.wireOp",EDGE,"E1.right");var subQ8=sQuery(id+"F0.wireOp",EDGE,"E1.top");var subQ9=sQuery(id+"F0.wireOp",EDGE,"E1.left");var subQ10=sQuery(id+"F0.wireOp",EDGE,"E23.filletArc");var subQ11=sQuery(id+"F0.wireOp",EDGE,"E24.filletArc");Q0=makeQuery(id+"F2.boolean.opBoolean","SPLIT",FACE,{"disambiguationData":[TD([makeQuery(id+"F1.opExtrude","SWEPT_FACE",FACE,{"disambiguationData":[OSD([subQ6])]})])],"derivedFrom":makeQuery(id+"F1.opExtrude","CAP_FACE",FACE,{"disambiguationData":[OSD([subQ6,subQ8,subQ9,subQ7,subQ4,subQ3,subQ2,subQ1,subQ0,subQ5,subQ10,subQ11])],"isStart":true})});}
            var sketch = newSketch(context, id + "F16", { "sketchPlane" : qUnion([Q0])});
            skPoint(sketch, "E79.start.orphan", {"position": v(0, 74.25) * mm});
            skLineSegment(sketch, "E80", {"start": v(0, 74.25) * mm, "end": v(0, 104.25) * mm, "construction": true});
            skCircle(sketch, "E81", {"center": v(0, 104.25) * mm, "radius": 6 * mm});
            skArc(sketch, "E82", {"start": v(15, 104.18) * mm, "mid": v(-0.2, 119.25) * mm, "end": v(-15, 103.8) * mm});
            skLineSegment(sketch, "E83", {"start": v(15, 104.18) * mm, "end": v(15, 92.25) * mm});
            skLineSegment(sketch, "E84", {"start": v(-15, 103.8) * mm, "end": v(-15, 92.25) * mm});
            skLineSegment(sketch, "E85", {"start": v(15, 92.25) * mm, "end": v(33, 74.25) * mm});
            skLineSegment(sketch, "E86", {"start": v(-15, 92.25) * mm, "end": v(-33, 74.25) * mm});
            skPoint(sketch, "E87.orphan", {"position": v(15, 74.25) * mm});
            skPoint(sketch, "E88.orphan", {"position": v(-15, 74.25) * mm});
            skLineSegment(sketch, "E89", {"start": v(-74.25, 0) * mm, "end": v(74.25, 0) * mm, "construction": true});
            skArc(sketch, "E90.MirrorCS", {"start": v(15, -104.18) * mm, "mid": v(-0.2, -119.25) * mm, "end": v(-15, -103.8) * mm});
            skLineSegment(sketch, "E91.MirrorCS", {"start": v(-15, -92.25) * mm, "end": v(-33, -74.25) * mm});
            skCircle(sketch, "E92.MirrorC", {"center": v(0, -104.25) * mm, "radius": 6 * mm});
            skLineSegment(sketch, "E93.MirrorCS", {"start": v(15, -92.25) * mm, "end": v(33, -74.25) * mm});
            skLineSegment(sketch, "E94.MirrorCS", {"start": v(0, -74.25) * mm, "end": v(0, -104.25) * mm, "construction": true});
            skLineSegment(sketch, "E95.MirrorCS", {"start": v(-15, -103.8) * mm, "end": v(-15, -92.25) * mm});
            skLineSegment(sketch, "E96.MirrorCS", {"start": v(15, -104.18) * mm, "end": v(15, -92.25) * mm});
            skSolve(sketch);
        }
        {
            var Q0;
            Q0=makeQuery(id+"F16.imprint","IMPRINT",FACE,{"disambiguationData":[TD([[makeQuery(id+"F16.imprint","IMPRINT",EDGE,{"derivedFrom":makeQuery(id+"F1.opExtrude","CAP_EDGE",EDGE,{"disambiguationData":[OSD([sQuery(id+"F0.wireOp",EDGE,"E1.left")])],"isStart":true})}),-1.0]])]});
            var Q1;
            Q1=makeQuery(id+"F16.imprint","IMPRINT",FACE,{"disambiguationData":[TD([[makeQuery(id+"F16.imprint","IMPRINT",EDGE,{"derivedFrom":sQuery(id+"F16.wireOp",EDGE,"E81")}),-1.0]])]});
            var Q2;
            Q2=makeQuery(id+"F16.imprint","IMPRINT",FACE,{"disambiguationData":[TD([[makeQuery(id+"F16.imprint","IMPRINT",EDGE,{"derivedFrom":sQuery(id+"F16.wireOp",EDGE,"E90.MirrorCS")}),-1.0]])]});
            var Q3;
            Q3=makeQuery(id+"F2.opExtrude","CAP_FACE",FACE,{"disambiguationData":[OSD([sQuery(id+"F0.wireOp",EDGE,"E12"),sQuery(id+"F0.wireOp",EDGE,"E13"),sQuery(id+"F0.wireOp",EDGE,"E14"),sQuery(id+"F0.wireOp",EDGE,"E15"),sQuery(id+"F0.wireOp",EDGE,"E17.filletArc"),sQuery(id+"F0.wireOp",EDGE,"E18.filletArc"),sQuery(id+"F0.wireOp",EDGE,"E19.filletArc"),sQuery(id+"F0.wireOp",EDGE,"E20.filletArc"),sQuery(id+"F0.wireOp",EDGE,"E25.0"),sQuery(id+"F0.wireOp",EDGE,"E25.1"),sQuery(id+"F0.wireOp",EDGE,"E25.2"),sQuery(id+"F0.wireOp",EDGE,"E25.3"),sQuery(id+"F0.wireOp",EDGE,"E25.4"),sQuery(id+"F0.wireOp",EDGE,"E25.5"),sQuery(id+"F0.wireOp",EDGE,"E25.6"),sQuery(id+"F0.wireOp",EDGE,"E25.7")])],"isStart":false});
            extrude(context, id + "F17", {"entities" : qUnion([Q0, Q1, Q2]), "endBound" : BoundingType.UP_TO_SURFACE, "depth" : 25.4 * mm, "endBoundEntityFace" : qUnion([Q3]), "offsetDistance" : 25.4 * mm});
        }
    });
